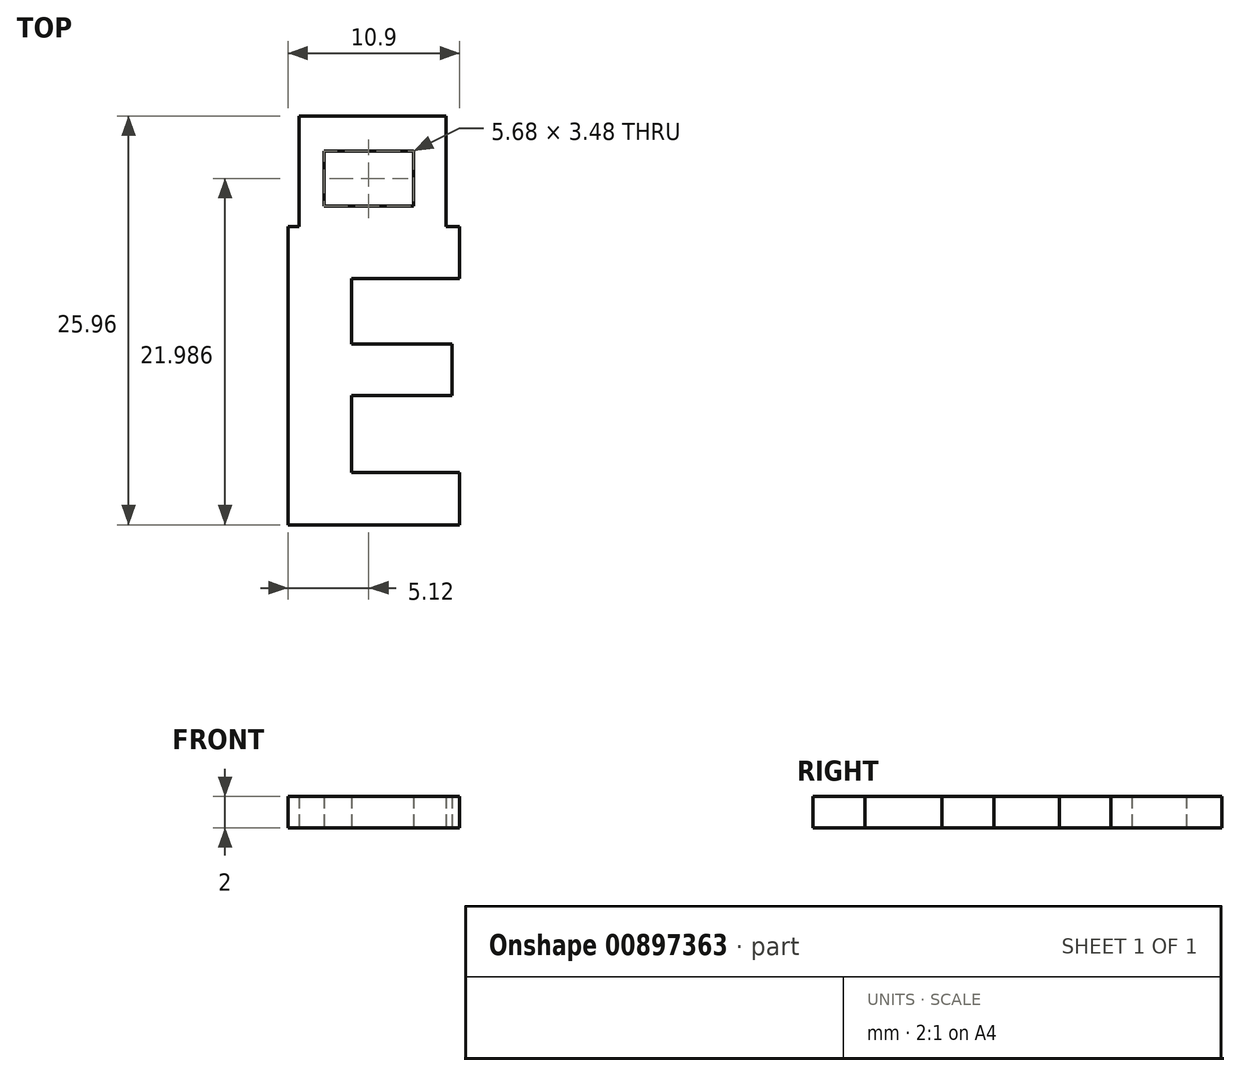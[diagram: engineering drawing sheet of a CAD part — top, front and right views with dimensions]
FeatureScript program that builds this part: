
annotation { "Feature Type Name" : "Feature", "Feature Type Description" : "" }
export const myFeature = defineFeature(function(context is Context, id is Id, definition is map)
    precondition{}
    {
        {
            var Q0;
            Q0=qCreatedBy(makeId("Top.planeOp"),FACE);
            var sketch = newSketch(context, id + "F0", { "sketchPlane" : qUnion([Q0])});
            skText(sketch, "E0", { "text": "E", "fontName": "OpenSans-Bold.ttf"});
            skLineSegment(sketch, "E1.bottom", {"start": v(3.1, -1.07) * mm, "end": v(12.43, -1.07) * mm});
            skLineSegment(sketch, "E1.top", {"start": v(3.1, 6.87) * mm, "end": v(12.43, 6.87) * mm});
            skLineSegment(sketch, "E1.left", {"start": v(3.1, -1.07) * mm, "end": v(3.1, 6.87) * mm});
            skLineSegment(sketch, "E1.right", {"start": v(12.43, -1.07) * mm, "end": v(12.43, 6.87) * mm});
            skLineSegment(sketch, "E2", {"start": v(7.5, -1.07) * mm, "end": v(7.5, 6.87) * mm});
            skPoint(sketch, "E2.startSnap0", {"position": v(7.76, -1.07) * mm});
            skPoint(sketch, "E2.endSnap0", {"position": v(7.76, 6.87) * mm});
            skLineSegment(sketch, "E3.bottom", {"start": v(10.34, 1.15) * mm, "end": v(4.66, 1.15) * mm});
            skLineSegment(sketch, "E3.top", {"start": v(10.34, 4.64) * mm, "end": v(4.66, 4.64) * mm});
            skLineSegment(sketch, "E3.left", {"start": v(10.34, 1.15) * mm, "end": v(10.34, 4.64) * mm});
            skLineSegment(sketch, "E3.right", {"start": v(4.66, 1.15) * mm, "end": v(4.66, 4.64) * mm});
            skPoint(sketch, "E3.middle", {"position": v(7.5, 2.9) * mm});
            const initialGuessF0  = {"E0": [0, -0.01909, 1, 0, 0.01909]};
            skSetInitialGuess(sketch, initialGuessF0);
            skSolve(sketch);
        }
        {
            var Q0;
            Q0 = qSketchRegion(id + "F0", true);
            extrude(context, id + "F1", {"entities" : qUnion([Q0]), "depth" : 2 * mm, "offsetDistance" : 25.4 * mm});
        }
    });
